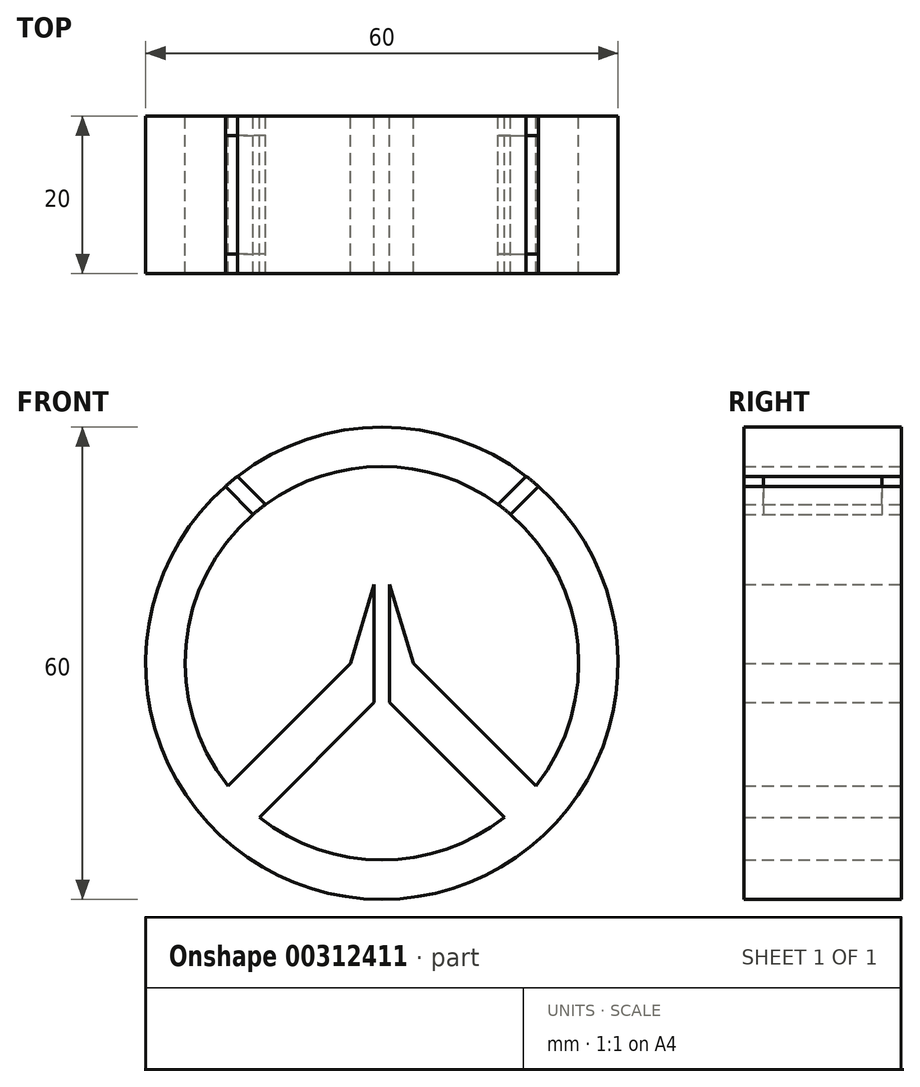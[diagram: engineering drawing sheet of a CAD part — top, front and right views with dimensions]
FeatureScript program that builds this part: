
annotation { "Feature Type Name" : "Feature", "Feature Type Description" : "" }
export const myFeature = defineFeature(function(context is Context, id is Id, definition is map)
    precondition{}
    {
        {
            var Q0;
            Q0=qCreatedBy(makeId("Front.planeOp"),FACE);
            var sketch = newSketch(context, id + "F0", { "sketchPlane" : qUnion([Q0])});
            skCircle(sketch, "E0", {"center": v(0, 0) * mm, "radius": 30 * mm});
            skLineSegment(sketch, "E1", {"start": v(-1, 10) * mm, "end": v(-1, -5) * mm});
            skLineSegment(sketch, "E2", {"start": v(1, 10) * mm, "end": v(1, -5) * mm});
            skArc(sketch, "E3", {"start": v(-15.56, -19.56) * mm, "mid": v(0, -25) * mm, "end": v(15.56, -19.56) * mm});
            skLineSegment(sketch, "E4", {"start": v(-1, 10) * mm, "end": v(-4, 0) * mm});
            skLineSegment(sketch, "E5", {"start": v(1, 10) * mm, "end": v(4, 0) * mm});
            skLineSegment(sketch, "E6", {"start": v(-1, -5) * mm, "end": v(-15.56, -19.56) * mm});
            skLineSegment(sketch, "E7", {"start": v(1, -5) * mm, "end": v(15.56, -19.56) * mm});
            skLineSegment(sketch, "E8.trimOffspring", {"start": v(4, 0) * mm, "end": v(19.56, -15.56) * mm});
            skLineSegment(sketch, "E9.trimOffspring", {"start": v(-4, 0) * mm, "end": v(-19.56, -15.56) * mm});
            skArc(sketch, "E10.trimOffspring", {"start": v(19.56, -15.56) * mm, "mid": v(0, 25) * mm, "end": v(-19.56, -15.56) * mm});
            skLineSegment(sketch, "E11", {"start": v(-14.76, 20.18) * mm, "end": v(-18.33, 23.75) * mm});
            skLineSegment(sketch, "E12", {"start": v(-19.88, 22.47) * mm, "end": v(-16.34, 18.92) * mm});
            skLineSegment(sketch, "E13", {"start": v(16.34, 18.92) * mm, "end": v(19.88, 22.47) * mm});
            skLineSegment(sketch, "E14", {"start": v(14.76, 20.18) * mm, "end": v(18.33, 23.75) * mm});
            skSolve(sketch);
        }
        {
            var Q0;
            Q0=makeQuery(id+"F0.imprint","IMPRINT",FACE,{"disambiguationData":[TD([[makeQuery(id+"F0.imprint","IMPRINT",EDGE,{"derivedFrom":sQuery(id+"F0.wireOp",EDGE,"E1")}),-1.0]])]});
            extrude(context, id + "F1", {"entities" : qUnion([Q0]), "endBound" : BoundingType.SYMMETRIC, "depth" : 20 * mm});
        }
        {
            var Q0;
            {var subQ0=sQuery(id+"F0.wireOp",EDGE,"E11");Q0=makeQuery(id+"F0.imprint","IMPRINT",FACE,{"disambiguationData":[TD([[makeQuery(id+"F0.imprint","IMPRINT",EDGE,{"derivedFrom":subQ0}),-1.0]])]});}
            extrude(context, id + "F2", {"entities" : qUnion([Q0]), "endBound" : BoundingType.SYMMETRIC, "depth" : 20 * mm});
        }
        {
            var Q0;
            {var subQ0=sQuery(id+"F0.wireOp",EDGE,"E13");Q0=makeQuery(id+"F0.imprint","IMPRINT",FACE,{"disambiguationData":[TD([[makeQuery(id+"F0.imprint","IMPRINT",EDGE,{"derivedFrom":subQ0}),1.0]])]});}
            var Q1;
            {var subQ0=sQuery(id+"F0.wireOp",EDGE,"E11");Q1=makeQuery(id+"F0.imprint","IMPRINT",FACE,{"disambiguationData":[TD([[makeQuery(id+"F0.imprint","IMPRINT",EDGE,{"derivedFrom":subQ0}),1.0]])]});}
            extrude(context, id + "F3", {"entities" : qUnion([Q0, Q1]), "endBound" : BoundingType.SYMMETRIC, "depth" : 15 * mm});
        }
    });
